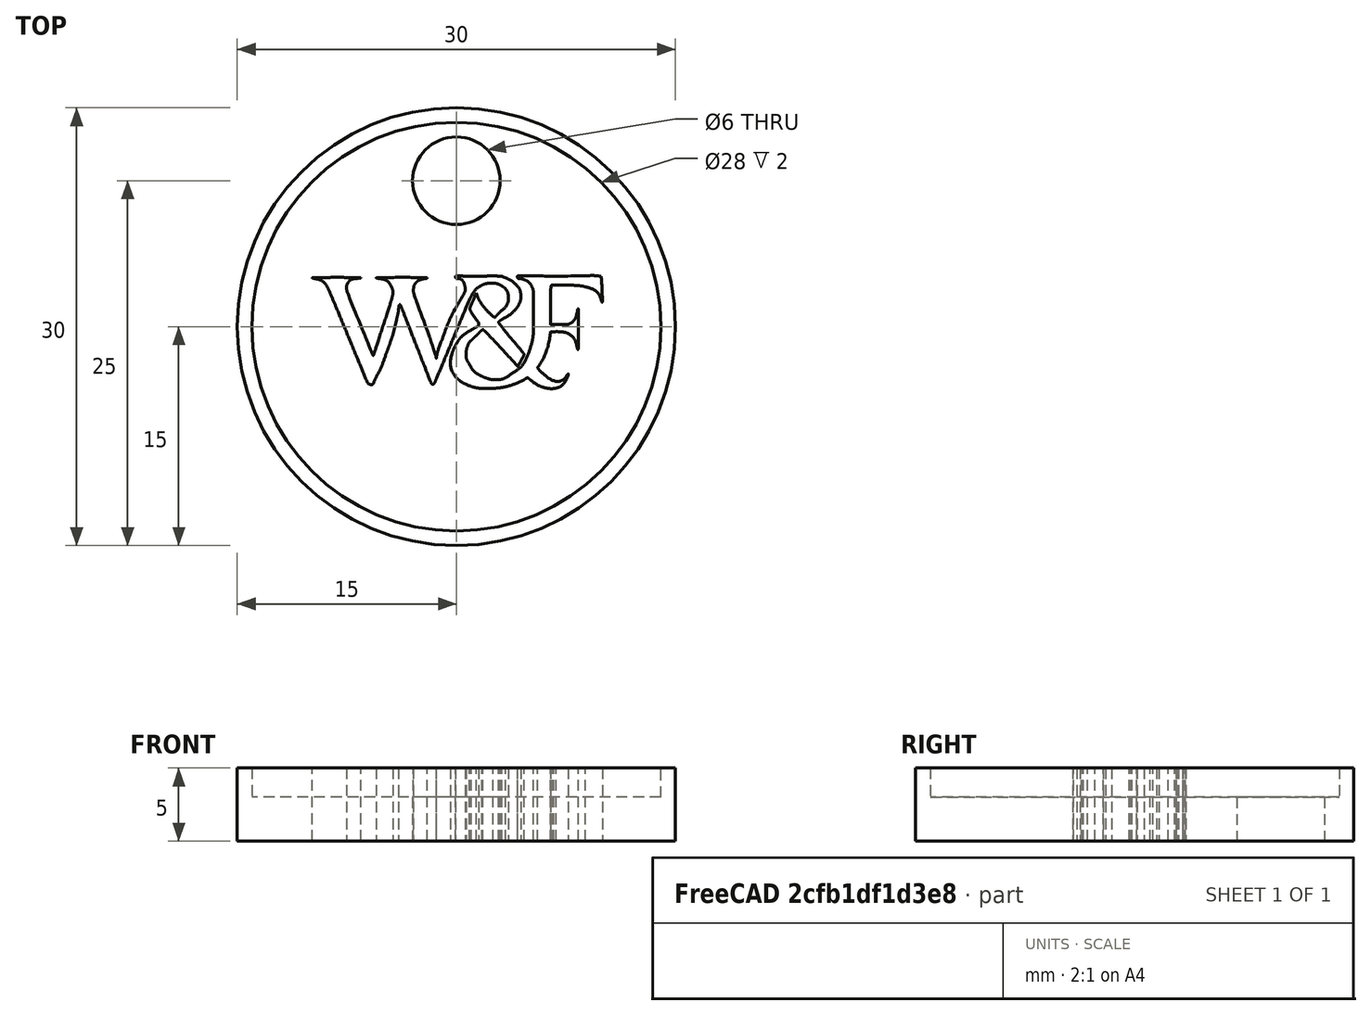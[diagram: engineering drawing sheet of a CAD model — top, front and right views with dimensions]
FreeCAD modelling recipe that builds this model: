
FCSTD DOCUMENT  (FreeCAD 0.20R29410 (Git))
Label: w&f
License: All rights reserved
LicenseURL: http://en.wikipedia.org/wiki/All_rights_reserved
objects: Part::Extrusion×3, Sketcher::SketchObject×2, Part::MultiFuse×1, Part::Cylinder×1, Part::Cut×1, Part::Feature×1
note: 9 computed .brp shape members not serialized (recipe doc carries the construction recipe); baked Part::Feature solids carry a one-line shape summary decoded from their .brp

FEATURE [Sketcher::SketchObject] Sketch
  FullyConstrained = true
  sketch-geometry (1):
    g0: Circle CenterX=0 CenterY=0 CenterZ=0 NormalX=0 NormalY=0 NormalZ=1 AngleXU=0 Radius=15
  constraints (2):
    c: Coincident(g0,g-1)
    c: Diameter(g0) = 30
FEATURE [Part::Extrusion] Extrude001
  Base = -> Sketch
  Dir = (0,0,1)
  DirMode = 0
  FaceMakerClass = Part::FaceMakerBullseye
  LengthFwd = 3
  LengthRev = 0
  Solid = true
  Symmetric = false
FEATURE [Sketcher::SketchObject] Sketch001
  FullyConstrained = true
  sketch-geometry (2):
    g0: Circle CenterX=0 CenterY=0 CenterZ=0 NormalX=0 NormalY=0 NormalZ=1 AngleXU=0 Radius=15
    g1: Circle CenterX=0 CenterY=0 CenterZ=0 NormalX=0 NormalY=0 NormalZ=1 AngleXU=0 Radius=14
  constraints (4):
    c: Coincident(g0,g-1)
    c: Diameter(g0) = 30
    c: Coincident(g1,g0)
    c: Diameter(g1) = 28
FEATURE [Part::Extrusion] Extrude002
  Base = -> Sketch001
  Dir = (0,0,1)
  DirMode = 0
  FaceMakerClass = Part::FaceMakerBullseye
  LengthFwd = 2
  LengthRev = 0
  Placement = pos=(0,0,3) rot=(0,0,1;0rad)
  Solid = true
  Symmetric = false
FEATURE [Part::MultiFuse] Fusion
  Refine = true
  Shapes = -> [Extrude002,Extrude001]
FEATURE [Part::Cylinder] Cylinder
  Angle = 360
  AttacherType = Attacher::AttachEngine3D
  FirstAngle = 0
  Height = 10
  Placement = pos=(0,10,0) rot=(0,0,1;0rad)
  Radius = 3
  SecondAngle = 0
FEATURE [Part::Cut] Cut
  Base = -> Fusion
  Refine = true
  Tool = -> Cylinder
FEATURE [Part::Feature] path24001
  shape: bbox 19.89 x 7.867 x 2e-07 mm, 1 faces, 0 solids (baked)
FEATURE [Part::Extrusion] Extrude
  Base = -> path24001
  Dir = (0,0,1)
  DirMode = 0
  FaceMakerClass = Part::FaceMakerBullseye
  LengthFwd = 5
  LengthRev = 0
  Solid = false
  Symmetric = false
